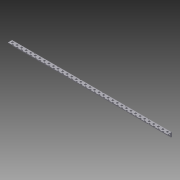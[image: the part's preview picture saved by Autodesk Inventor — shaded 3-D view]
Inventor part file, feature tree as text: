
AUTODESK INVENTOR PART (.ipt)
format: ipt  version: 2014 SP1 (Build 180222100, 222)  size: 2,041,856 bytes
history: native  units: in
note: dims shown in document units (in); Inventor stores cm internally (conversion verified against a paired STEP export)
features: other x1, imported_body x1, extrude x1, sketch x1, projected_geometry x1
ambient origin geometry x8: Origin, YZ Plane, XZ Plane, XY Plane, X Axis, Y Axis, Z Axis, Center Point
bodies: Body1 (feature_tree)
feature tree (5):
  parser-record x1  (decoder bookkeeping rows leaked as tree rows — omitted from the tree; the rows remain in map.json)
  imported_body  "Base1"
  extrude  "Extrusion1"  Depth=1.0in TaperAngle=0.0deg
  sketch  "Sketch1"  dims[d1=0.5in d2=1.0in d3=0.0in]
  projected_geometry  "Projected Loop1"
